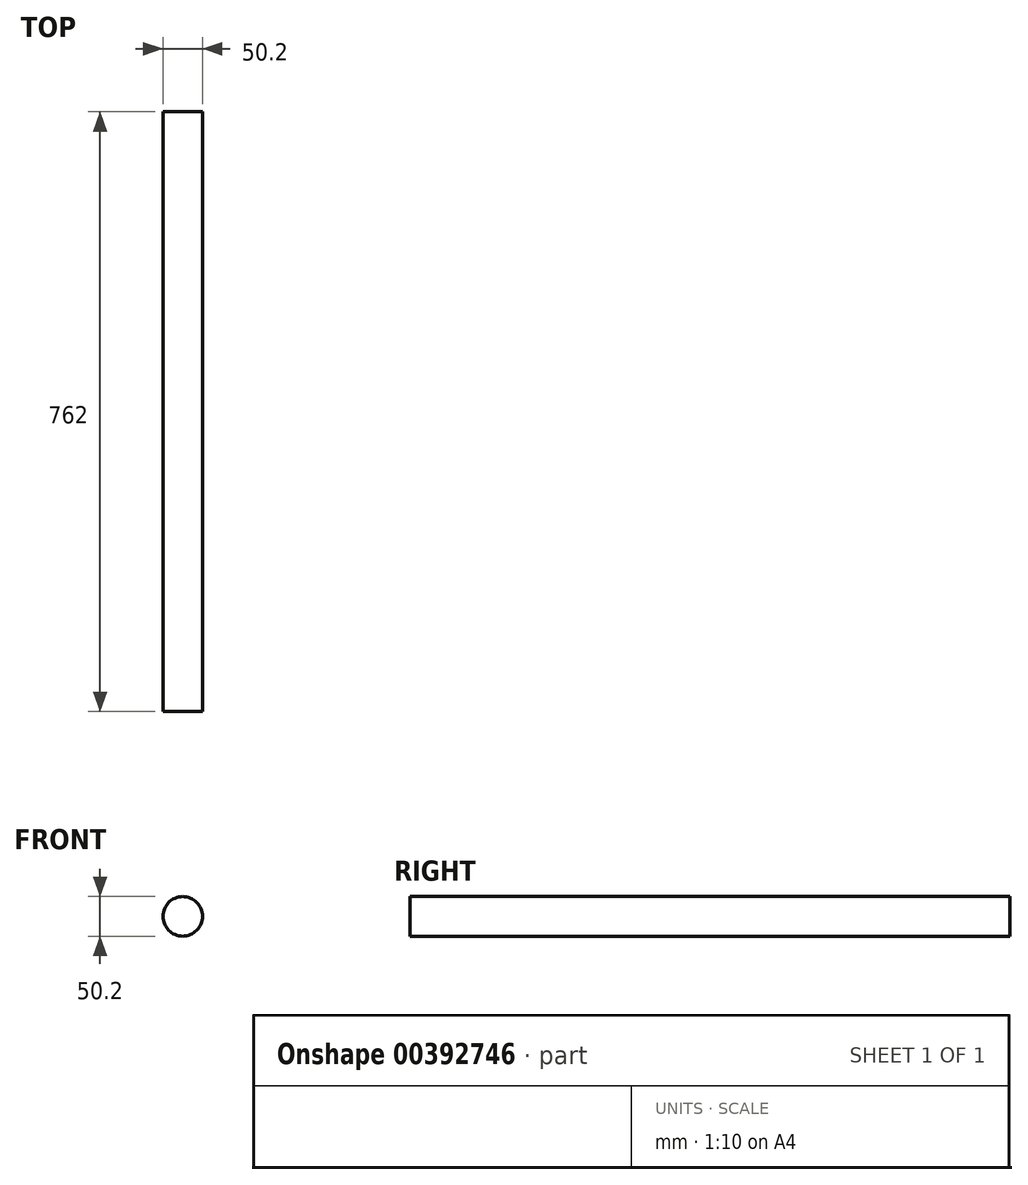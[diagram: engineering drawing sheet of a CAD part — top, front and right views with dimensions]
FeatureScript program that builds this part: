
annotation { "Feature Type Name" : "Feature", "Feature Type Description" : "" }
export const myFeature = defineFeature(function(context is Context, id is Id, definition is map)
    precondition{}
    {
        {
            var Q0;
            Q0=qCreatedBy(makeId("Front.planeOp"),FACE);
            var sketch = newSketch(context, id + "F0", { "sketchPlane" : qUnion([Q0])});
            skCircle(sketch, "E0", {"center": v(0, 0) * mm, "radius": 25.1 * mm});
            skSolve(sketch);
        }
        {
            var Q0;
            Q0 = qSketchRegion(id + "F0", true);
            extrude(context, id + "F1", {"entities" : qUnion([Q0]), "endBound" : BoundingType.SYMMETRIC, "depth" : 762 * mm});
        }
    });
